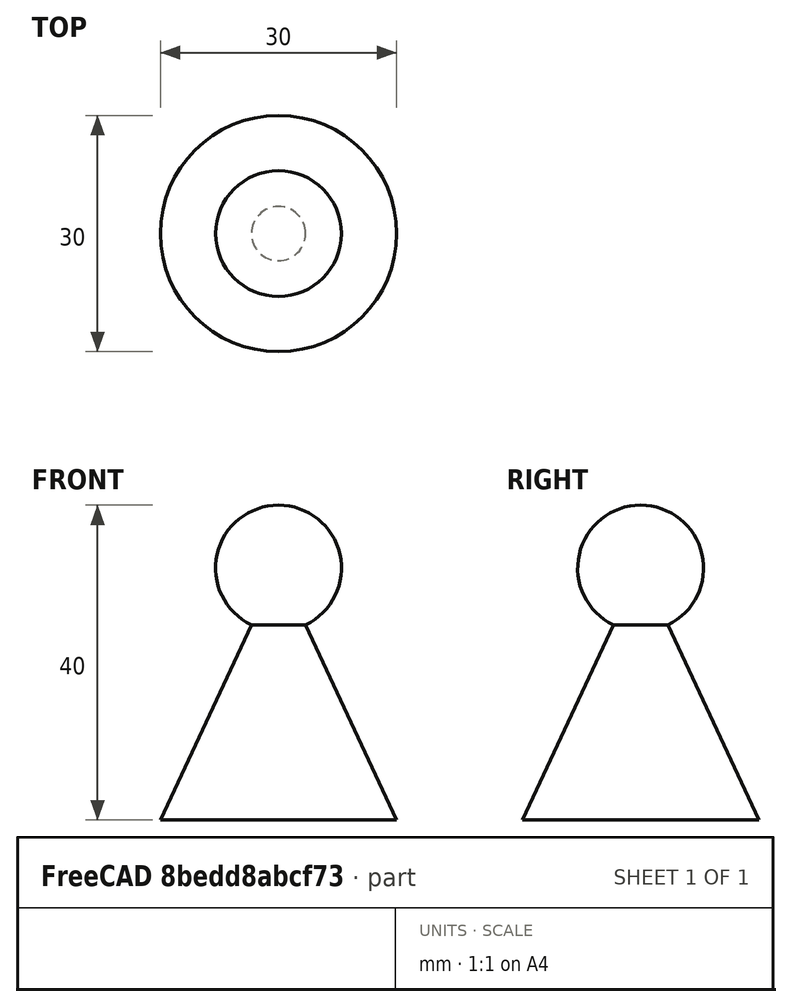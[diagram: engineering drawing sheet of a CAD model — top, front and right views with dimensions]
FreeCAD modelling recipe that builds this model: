
FCSTD DOCUMENT  (FreeCAD 0.16R6707 (Git))
Label: 05-ficha
License: All rights reserved
LicenseURL: http://en.wikipedia.org/wiki/All_rights_reserved
objects: Sketcher::SketchObject×1, PartDesign::Revolution×1
note: 3 computed .brp shape members not serialized (recipe doc carries the construction recipe); baked Part::Feature solids carry a one-line shape summary decoded from their .brp

FEATURE [Sketcher::SketchObject] Sketch
  Placement = pos=(0,0,0) rot=(-1,0,0;4.71239rad)
  sketch-geometry (4):
    g0: ArcOfCircle CenterX=0 CenterY=32 CenterZ=0 NormalX=0 NormalY=0 NormalZ=1 Radius=8 StartAngle=5.15758 EndAngle=7.85398
    g1: LineSegment StartX=0 StartY=40 StartZ=0 EndX=0 EndY=0 EndZ=0
    g2: LineSegment StartX=0 StartY=0 StartZ=0 EndX=15 EndY=0 EndZ=0
    g3: LineSegment StartX=15 StartY=0 StartZ=0 EndX=3.44501 EndY=24.7798 EndZ=0
  constraints (12):
    c: Coincident(g0,g1)
    c: Coincident(g1,g2)
    c: Horizontal(g2)
    c: Coincident(g2,g3)
    c: Coincident(g3,g0)
    c: Coincident(g1,g-1)
    c: Vertical(g1)
    c: PointOnObject(g0,g1)
    c: DistanceY(g1,g1) = 40
    c: DistanceX(g2,g2) = 15
    c: Radius(g0) = 8
    c: Angle(g3,g2) = 1.13446
FEATURE [PartDesign::Revolution] Revolution
  Angle = 360
  Axis = (0,0,1)
  Base = (0,0,0)
  Placement = pos=(0,0,0) rot=(-1,0,0;4.71239rad)
  ReferenceAxis = -> Sketch [V_Axis]
  Sketch = -> Sketch
